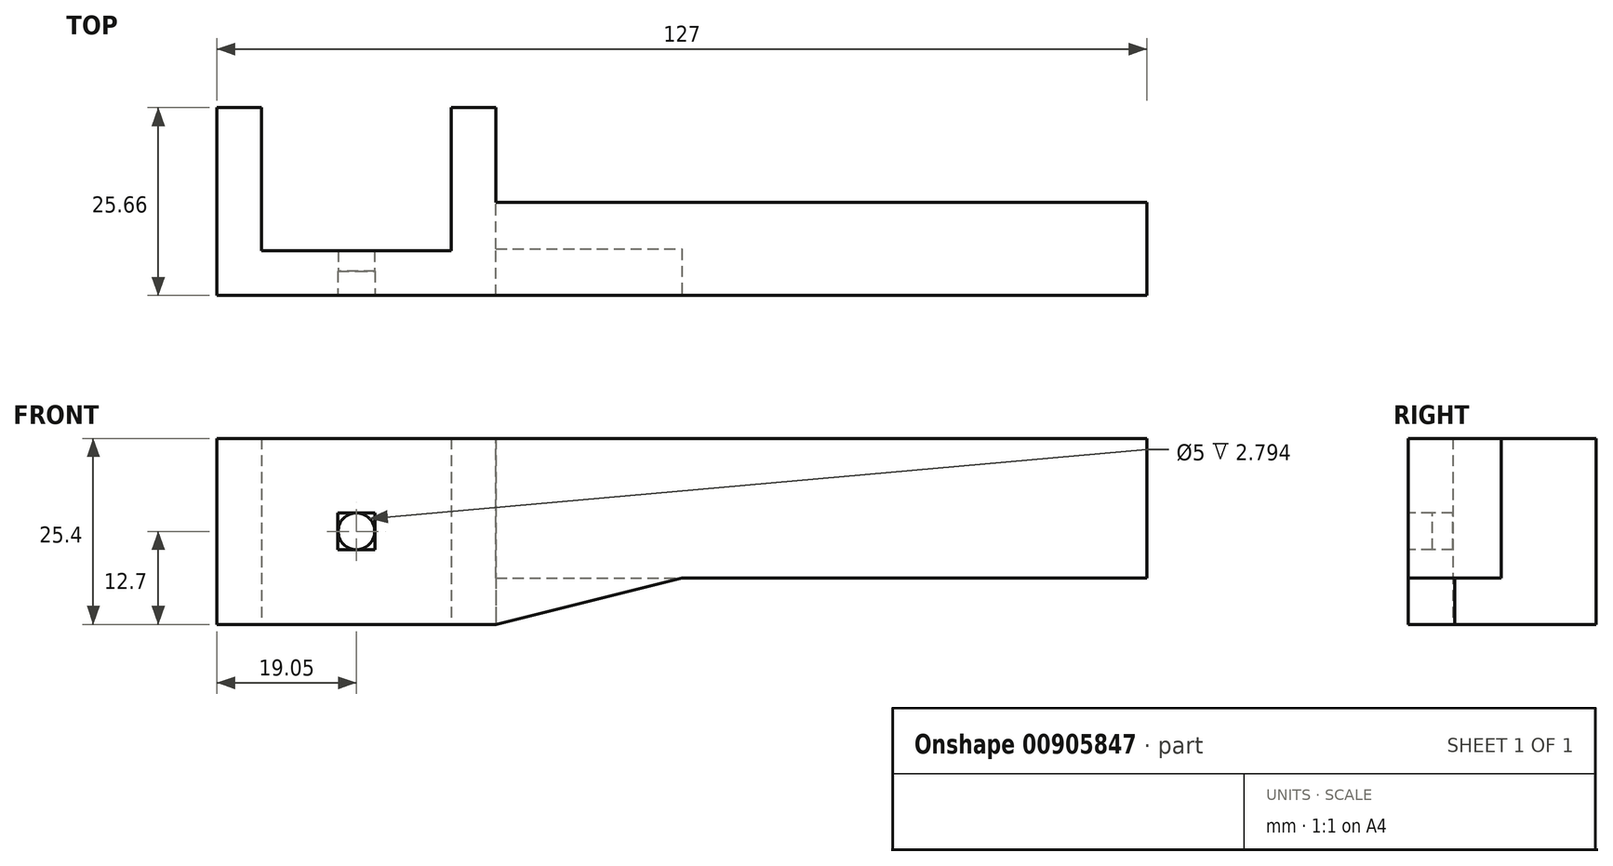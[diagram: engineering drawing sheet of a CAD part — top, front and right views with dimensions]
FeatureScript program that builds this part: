
annotation { "Feature Type Name" : "Feature", "Feature Type Description" : "" }
export const myFeature = defineFeature(function(context is Context, id is Id, definition is map)
    precondition{}
    {
        {
            var Q0;
            Q0=qCreatedBy(makeId("Top.planeOp"),FACE);
            var sketch = newSketch(context, id + "F0", { "sketchPlane" : qUnion([Q0])});
            skLineSegment(sketch, "E0.bottom", {"start": v(12.95, -9.78) * mm, "end": v(-12.95, -9.78) * mm});
            skLineSegment(sketch, "E0.top", {"start": v(12.95, 9.78) * mm, "end": v(6.35, 9.78) * mm});
            skLineSegment(sketch, "E0.left", {"start": v(12.95, -9.78) * mm, "end": v(12.95, 9.78) * mm});
            skLineSegment(sketch, "E0.right", {"start": v(-12.95, -9.78) * mm, "end": v(-12.95, 9.78) * mm});
            skPoint(sketch, "E0.middle", {"position": v(0, 0) * mm});
            skLineSegment(sketch, "E1.1", {"start": v(19.05, -15.87) * mm, "end": v(19.05, 9.78) * mm});
            skLineSegment(sketch, "E1.2", {"start": v(19.05, -15.87) * mm, "end": v(-19.05, -15.88) * mm});
            skLineSegment(sketch, "E1.3", {"start": v(-19.05, -15.88) * mm, "end": v(-19.05, 9.78) * mm});
            skLineSegment(sketch, "E2.top", {"start": v(-5.84, 3.94) * mm, "end": v(6.35, 3.94) * mm});
            skLineSegment(sketch, "E2.left", {"start": v(-5.84, 9.78) * mm, "end": v(-5.84, 3.94) * mm});
            skLineSegment(sketch, "E2.right", {"start": v(6.35, 9.78) * mm, "end": v(6.35, 3.94) * mm});
            skLineSegment(sketch, "E3.trimOffspring", {"start": v(-5.84, 9.78) * mm, "end": v(-12.95, 9.78) * mm});
            skLineSegment(sketch, "E4", {"start": v(-19.05, 9.78) * mm, "end": v(-19.05, -15.88) * mm});
            skLineSegment(sketch, "E5", {"start": v(-12.95, 9.78) * mm, "end": v(-19.05, 9.78) * mm});
            skLineSegment(sketch, "E6", {"start": v(12.95, 9.78) * mm, "end": v(19.05, 9.78) * mm});
            skPoint(sketch, "E7.orphan", {"position": v(-19.05, 15.87) * mm});
            skSolve(sketch);
        }
        {
            var Q0;
            Q0=makeQuery(id+"F0.imprint","IMPRINT",FACE,{"disambiguationData":[TD([[makeQuery(id+"F0.imprint","IMPRINT",EDGE,{"derivedFrom":sQuery(id+"F0.wireOp",EDGE,"E0.bottom")}),1.0]])]});
            extrude(context, id + "F1", {"entities" : qUnion([Q0]), "depth" : 25.4 * mm, "offsetDistance" : 25.4 * mm, "symmetric" : true});
        }
        {
            var Q0;
            Q0=makeQuery(id+"F1.opExtrude","SWEPT_FACE",FACE,{"disambiguationData":[OSD([sQuery(id+"F0.wireOp",EDGE,"E1.2")])]});
            var sketch = newSketch(context, id + "F2", { "sketchPlane" : qUnion([Q0])});
            skCircle(sketch, "E8", {"center": v(0, 0) * mm, "radius": 2.5 * mm});
            skSolve(sketch);
        }
        {
            var Q0;
            Q0=makeQuery(id+"F2.imprint","IMPRINT",FACE,{"disambiguationData":[TD([[makeQuery(id+"F2.imprint","IMPRINT",EDGE,{"derivedFrom":sQuery(id+"F2.wireOp",EDGE,"E8")}),1.0]])]});
            extrude(context, id + "F3", {"entities" : qUnion([Q0]), "operationType" : NewBodyOperationType.REMOVE, "endBound" : BoundingType.THROUGH_ALL, "oppositeDirection" : true, "depth" : 25.4 * mm, "offsetDistance" : 25.4 * mm});
        }
        {
            var Q0;
            Q0=makeQuery(id+"F1.opExtrude","SWEPT_FACE",FACE,{"disambiguationData":[OSD([sQuery(id+"F0.wireOp",EDGE,"E1.2")])]});
            var sketch = newSketch(context, id + "F4", { "sketchPlane" : qUnion([Q0])});
            skLineSegment(sketch, "E9.bottom", {"start": v(2.53, -2.53) * mm, "end": v(-2.53, -2.53) * mm});
            skLineSegment(sketch, "E9.top", {"start": v(2.53, 2.53) * mm, "end": v(-2.53, 2.53) * mm});
            skLineSegment(sketch, "E9.left", {"start": v(2.53, -2.53) * mm, "end": v(2.53, 2.53) * mm});
            skLineSegment(sketch, "E9.right", {"start": v(-2.53, -2.53) * mm, "end": v(-2.53, 2.53) * mm});
            skPoint(sketch, "E9.middle", {"position": v(0, 0) * mm});
            skSolve(sketch);
        }
        {
            var Q0;
            Q0=qSketchRegion(id+"F4",true);
            extrude(context, id + "F5", {"entities" : qUnion([Q0]), "operationType" : NewBodyOperationType.REMOVE, "oppositeDirection" : true, "depth" : 3.3 * mm, "offsetDistance" : 25.4 * mm});
        }
        {
            var Q0;
            Q0=makeQuery(id+"F1.opExtrude","CAP_FACE",FACE,{"disambiguationData":[OSD([sQuery(id+"F0.wireOp",EDGE,"E0.bottom"),sQuery(id+"F0.wireOp",EDGE,"E0.top"),sQuery(id+"F0.wireOp",EDGE,"E0.left"),sQuery(id+"F0.wireOp",EDGE,"E0.right"),sQuery(id+"F0.wireOp",EDGE,"E1.0"),sQuery(id+"F0.wireOp",EDGE,"E1.1"),sQuery(id+"F0.wireOp",EDGE,"E1.2"),sQuery(id+"F0.wireOp",EDGE,"E2.top"),sQuery(id+"F0.wireOp",EDGE,"E2.left"),sQuery(id+"F0.wireOp",EDGE,"E2.right"),sQuery(id+"F0.wireOp",EDGE,"E3.trimOffspring"),sQuery(id+"F0.wireOp",EDGE,"E4")])],"isStart":false});
            var sketch = newSketch(context, id + "F6", { "sketchPlane" : qUnion([Q0])});
            skLineSegment(sketch, "E10.bottom", {"start": v(19.05, -3.17) * mm, "end": v(107.95, -3.17) * mm});
            skLineSegment(sketch, "E10.top", {"start": v(19.05, -15.87) * mm, "end": v(107.95, -15.87) * mm});
            skLineSegment(sketch, "E10.left", {"start": v(19.05, -3.17) * mm, "end": v(19.05, -15.87) * mm});
            skLineSegment(sketch, "E10.right", {"start": v(107.95, -3.17) * mm, "end": v(107.95, -15.87) * mm});
            skSolve(sketch);
        }
        {
            var Q0;
            Q0=makeQuery(id+"F6.imprint","IMPRINT",FACE,{"disambiguationData":[TD([[makeQuery(id+"F6.imprint","IMPRINT",EDGE,{"derivedFrom":sQuery(id+"F6.wireOp",EDGE,"E10.bottom")}),-1.0]])]});
            extrude(context, id + "F7", {"entities" : qUnion([Q0]), "operationType" : NewBodyOperationType.ADD, "oppositeDirection" : true, "depth" : 19.05 * mm, "offsetDistance" : 25.4 * mm});
        }
        {
            var Q0;
            Q0=makeQuery(id+"F7.boolean.opBoolean","MERGE",FACE,{"derivedFrom":[makeQuery(id+"F1.opExtrude","SWEPT_FACE",FACE,{"disambiguationData":[OSD([sQuery(id+"F0.wireOp",EDGE,"E1.2")])]}),makeQuery(id+"F7.opExtrude","SWEPT_FACE",FACE,{"disambiguationData":[OSD([sQuery(id+"F6.wireOp",EDGE,"E10.top")])]})]});
            var sketch = newSketch(context, id + "F8", { "sketchPlane" : qUnion([Q0])});
            skLineSegment(sketch, "E11", {"start": v(19.05, -12.7) * mm, "end": v(19.05, -6.35) * mm});
            skLineSegment(sketch, "E12", {"start": v(19.05, -6.35) * mm, "end": v(44.45, -6.35) * mm});
            skLineSegment(sketch, "E13", {"start": v(44.45, -6.35) * mm, "end": v(19.05, -12.7) * mm});
            skSolve(sketch);
        }
        {
            var Q0;
            Q0=qSketchRegion(id+"F8",true);
            extrude(context, id + "F9", {"entities" : qUnion([Q0]), "operationType" : NewBodyOperationType.ADD, "oppositeDirection" : true, "depth" : 6.35 * mm, "offsetDistance" : 25.4 * mm});
        }
    });
